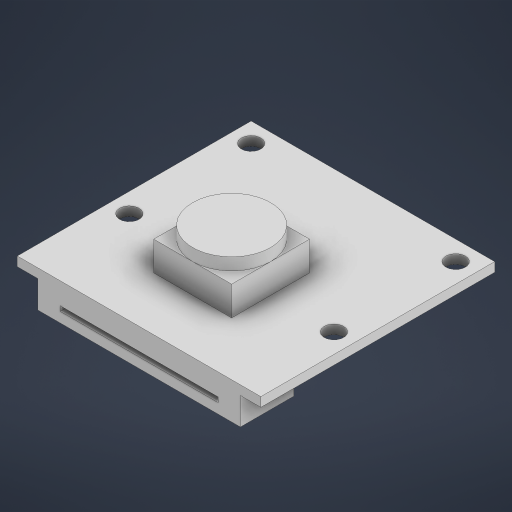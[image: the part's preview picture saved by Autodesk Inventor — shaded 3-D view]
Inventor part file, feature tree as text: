
AUTODESK INVENTOR PART (.ipt)
format: ipt  version: 2024 (Build 280153000, 153)  size: 249,344 bytes
history: native  units: mm
features: extrude x5, sketch x2, other x1
ambient origin geometry x8: Origin, YZ Plane, XZ Plane, XY Plane, X Axis, Y Axis, Z Axis, Center Point
bodies: Body1 (feature_tree)
feature tree (8):
  other  "솔리드1"
  sketch  "스케치1"
  extrude  "돌출1"  Depth=25.0mm
  extrude  "돌출2"  Depth=24.0mm
  extrude  "돌출3"  Depth=2.0mm
  extrude  "돌출4"  Depth=2.0mm
  extrude  "돌출5"  Depth=2.0mm
  sketch  "스케치2"
